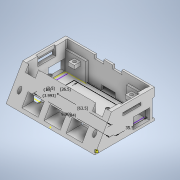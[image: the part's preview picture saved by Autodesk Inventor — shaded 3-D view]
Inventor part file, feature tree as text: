
AUTODESK INVENTOR PART (.ipt)
format: ipt  version: 2021 (Build 250183000, 183)  size: 608,256 bytes
history: native  units: mm
features: extrude x26, sketch x26, thread x2, projected_geometry x2, other x1, fillet x1
ambient origin geometry x8: Origin, YZ Plane, XZ Plane, XY Plane, X Axis, Y Axis, Z Axis, Center Point
bodies: Body1 (feature_tree)
feature tree (58):
  other  "Sólido1"
  extrude  "Extrusion Base"  Depth=2.0mm TaperAngle=0.0deg
  extrude  "Extrusión Angulo parte de adelante"  Depth=100.0mm TaperAngle=0.0deg
  extrude  "parte trasera diseño"  Depth=30.0mm TaperAngle=0.0deg
  extrude  "Extrusión parte trasera diseño con empalmes"  Depth=23.0mm
  fillet  "Empalme parte trasera diseño"  Radius=19.0mm
  extrude  "Parte delantera de la parte trasera diseño"  Depth=2.0mm
  extrude  "Extrusión Parte delantera de la parte trasera del diseño"  Depth=2.5mm
  extrude  "Extrusión Parte Trasera De la Parte trasera diseño"  Depth=2.5mm
  extrude  "Grado de inclinacion de 60.5 de parte delantera"  Depth=67.77mm TaperAngle=0.0deg
  extrude  "Lateral derecha de diseño"  Depth=10.0mm
  extrude  "Parte delantera diseño"  Depth=2.0mm
  extrude  "Lateral izquierda diseño"  Depth=4.0mm TaperAngle=0.0deg
  extrude  "Extrusion para placa trasera"  Depth=4.0mm
  extrude  "Extrusion capa parte delantera"  Depth=30.0mm
  extrude  "Extrusión huecos tornillos parte delantera"  Depth=22.142992mm
  extrude  "Tornillos Placa"  Depth=7.5mm TaperAngle=0.0deg
  thread  "Rosca1"  [1 undecoded]
  thread  "Rosca2"  [1 undecoded]
  extrude  "Extrusión sensores laterales"  Depth=3.5mm TaperAngle=0.0deg
  extrude  "Extrusión agujero cables inferiores"  Depth=30.0mm
  extrude  "Extrusión sensores delanteros"  Depth=4.5mm
  extrude  "Extrusión pads tornillos traseros placa"  Depth=30.0mm TaperAngle=0.0deg
  extrude  "Extrusión tornillos"  Depth=3.0mm
  extrude  "Extrusión tapa agujero"  Depth=18.0mm
  extrude  "Extrusión salida"  Depth=12.0mm TaperAngle=0.0deg
  extrude  "Extrusión desnivel"  Depth=5.0mm
  extrude  "Extrusión pared bateria"  Depth=18.5mm
  extrude  "Extrusión arreglo sensores"  Depth=3.0mm TaperAngle=0.0deg
  extrude  "Extrusión desnivel sensores"  Depth=18.0mm
  sketch  "Boceto placa"  dims[d143=59.5mm d144=18.0mm d145=12.0mm d146=1.0mm d147=11.5mm d148=1.0mm d149=12.0mm d150=18.0mm d151=6.4mm d152=6.4mm d153=1.0mm d154=18.0mm d155=12.0mm d156=19.25mm d157=0.0mm d158=18.0mm d159=4.0mm d160=7.0mm d161=10.0mm d162=7.0mm d163=0.0mm d164=3.5mm d165=4.75mm d166=0.0mm d167=63.5mm d168=26.5mm d172=84.0mm d176=10.0mm d177=3.993mm d178=3.5mm d179=35.5mm d180=9.069006mm d181=15.0mm d182=20.0mm d183=12.562006mm d184=2.0mm d185=2.0mm d186=10.0mm d187=0.0mm d188=0.0mm d189=0.0mm d190=3.0mm d191=0.0mm d192=123.5mm d193=0.0mm d194=20.0mm d195=0.0mm d198=13.0mm d199=64.0mm d200=13.0mm d201=1.0mm d202=9.5mm d203=7.0mm d204=0.0mm d210=0.0mm d219=87.0mm d220=21.0mm d221=12.0mm d222=23.0mm d223=98.0mm d224=7.5mm d225=7.5mm d226=79.5mm d229=2.1mm d230=9.0mm d231=11.0mm d232=16.0mm d235=1.0mm d236=3.6mm d239=2.1mm d241=1.3mm d242=5.0mm d243=36.0mm d244=9.5mm d245=5.0mm d246=17.0mm d247=10.0mm d252=8.7mm d254=4.3mm d255=4.0mm d256=11.0mm d257=54.0mm d258=2.85mm d259=11.0mm d262=2.2mm d263=1.3mm d264=4.3mm d265=85.25mm d266=0.0mm d268=2.0mm d269=0.0mm d270=2.15mm d271=1.0mm d105=0.5mm d106=0.872665mm d107=0.5mm d108=0.872665mm d248=0.5mm d249=0.872665mm d250=0.5mm d251=0.872665mm d253=0.872665mm d272=0.5mm d273=0.872665mm]
  sketch  "Boceto2"  dims[d6=3.5mm d22=2.0mm d23=0.0mm]
  sketch  "Boceto4"  dims[d24=20.935224mm d25=100.0mm d26=0.0mm]
  sketch  "Boceto5"  dims[d27=4.5mm d28=30.0mm d29=0.0mm]
  sketch  "Boceto6"  dims[d30=3.33mm d31=23.0mm d32=19.0mm]
  sketch  "Boceto7"  dims[d33=2.5mm d34=0.0mm d35=2.0mm]
  sketch  "Boceto8"  dims[d36=26.615mm d37=2.5mm]
  sketch  "Boceto9"  dims[d38=30.0mm d39=0.0mm d40=2.5mm]
  sketch  "Boceto10"  dims[d41=21.0mm d42=67.77mm d43=23.15mm d44=0.0mm d45=0.0mm]
  sketch  "Boceto11"  dims[d46=34.0mm d47=10.0mm]
  projected_geometry  "Contorno proyectado1"
  sketch  "Boceto13"  dims[d48=2.0mm d49=2.0mm]
  sketch  "Boceto14"  dims[d50=4.0mm d51=0.0mm d52=4.0mm d53=0.0mm]
  sketch  "Boceto15"  dims[d54=4.0mm d55=0.0mm d56=4.0mm]
  projected_geometry  "Contorno proyectado2"
  sketch  "Boceto17"  dims[d57=30.0mm d58=0.0mm d59=10.480702mm]
  sketch  "Boceto24"  dims[d60=103.25mm d61=0.0mm d62=22.142992mm]
  sketch  "Boceto25"  dims[d63=57.5mm d64=0.0mm d65=93.0mm d66=0.0mm d67=7.5mm d68=7.5mm]
  sketch  "Boceto26"  dims[d69=3.5mm d70=90.25mm d71=0.0mm]
  sketch  "Boceto27"  dims[d120=13.0mm d121=30.0mm]
  sketch  "Boceto28"  dims[d122=3.5mm d123=4.5mm]
  sketch  "Boceto29"  dims[d124=18.0mm d125=0.0mm d126=30.0mm d127=0.0mm]
  sketch  "Boceto32"  dims[d128=30.0mm d129=0.0mm d130=3.0mm]
  sketch  "Boceto33"  dims[d131=3.0mm d132=18.0mm]
  sketch  "Boceto34"  dims[d133=12.0mm d134=98.25mm d135=0.0mm]
  sketch  "Boceto36"  dims[d136=15.0mm d137=5.0mm]
  sketch  "Boceto39"  dims[d138=0.0mm d139=18.5mm]
  sketch  "Boceto40"  dims[d140=18.5mm d141=3.0mm d142=0.0mm]
note: 2 required parameter values undecoded (feature->parameter linkage not recoverable at this tier; creation-order binding heuristic only, values carry confidence <= 0.55)
